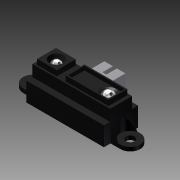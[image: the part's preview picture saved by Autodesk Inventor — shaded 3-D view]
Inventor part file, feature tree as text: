
AUTODESK INVENTOR PART (.ipt)
format: ipt  version: 2012 (Build 160160000, 160)  size: 424,448 bytes
history: native  units: mm
features: sketch x27, extrude x17, plane x3, mirror x3, revolve x3, loft x2, projected_geometry x2
ambient origin geometry x8: Origin, YZ Plane, XZ Plane, XY Plane, X Axis, Y Axis, Z Axis, Center Point
bodies: Solid1 (feature_tree)
feature tree (57):
  extrude  "Extrusion1"  Depth=13.0mm
  extrude  "Extrusion2"  Depth=4.2mm
  extrude  "Extrusion3"  Depth=6.3mm TaperAngle=0.0deg
  extrude  "Extrusion4"  Depth=7.2mm
  extrude  "Extrusion5"  Depth=1.2mm
  extrude  "Extrusion6"  Depth=2.0mm TaperAngle=0.0deg
  extrude  "Extrusion7"  Depth=7.5mm
  sketch  "Sketch8"  dims[d18=2.0mm d19=0.0mm d20=6.3mm d21=0.0mm]
  sketch  "Sketch9"  dims[d22=3.75mm d23=3.2mm]
  plane  "Work Plane1"
  extrude  "Extrusion8"  Depth=6.3mm TaperAngle=0.0deg
  extrude  "Extrusion9"  Depth=3.2mm
  plane  "Work Plane2"
  mirror  "Mirror1"
  loft  "Loft1"
  sketch  "Sketch14"  dims[d36=0.0mm d37=90.0deg d38=90.0deg]
  plane  "Work Plane3"
  revolve  "Revolution1"  [1 undecoded]
  revolve  "Revolution2"  [1 undecoded]
  extrude  "Extrusion10"  TaperAngle=0.0deg  [1 undecoded]
  loft  "Loft2"
  extrude  "Extrusion11"  Depth=0.5mm
  revolve  "Revolution3"  [1 undecoded]
  extrude  "Extrusion12"  Depth=1.5mm TaperAngle=0.0deg
  extrude  "Extrusion13"  Depth=4.2mm
  mirror  "Mirror2"
  extrude  "Extrusion14"  TaperAngle=0.0deg  [1 undecoded]
  extrude  "Extrusion15"  TaperAngle=90.0deg  [1 undecoded]
  mirror  "Mirror3"
  extrude  "Extrusion16"  Depth=5.05mm
  extrude  "Extrusion17"  Depth=5.9mm TaperAngle=0.0deg
  sketch  "Sketch1"  dims[d0=29.5mm d1=13.0mm]
  sketch  "Sketch2"  dims[d2=13.5mm d3=0.0mm d4=4.2mm]
  sketch  "Sketch3"  dims[d5=8.4mm d6=6.3mm d7=0.0mm]
  sketch  "Sketch4"  dims[d8=3.6mm d9=7.2mm]
  sketch  "Sketch5"  dims[d10=2.0mm d11=0.0mm d12=1.2mm]
  sketch  "Sketch6"  dims[d13=1.2mm d14=2.0mm d15=0.0mm]
  sketch  "Sketch7"  dims[d16=16.3mm d17=7.5mm]
  sketch  "Sketch10"  dims[d24=1.5mm d25=0.0mm d26=2.6mm]
  sketch  "Sketch11"  dims[d27=5.0mm d28=1.5mm d29=0.0mm]
  sketch  "Sketch12"  dims[d30=1.5mm d31=0.0mm d32=1.0mm]
  sketch  "Sketch13"  dims[d33=3.5mm d34=0.0mm d35=90.0deg]
  sketch  "Sketch15"  dims[d39=90.0deg d40=0.5mm]
  sketch  "Sketch16"  dims[d41=0.5mm d42=0.5mm]
  sketch  "Sketch17"  dims[d43=0.5mm d44=1.5mm d45=0.0mm]
  sketch  "Sketch18"  dims[d46=6.2mm d47=4.2mm]
  projected_geometry  "Projected Loop1"
  sketch  "Sketch19"  dims[d48=0.0mm d49=90.0deg d50=0.0mm d51=90.0deg]
  sketch  "Sketch20"  dims[d52=0.5mm d53=0.0mm d54=90.0deg]
  sketch  "Sketch21"  dims[d55=3.3mm d56=5.05mm]
  projected_geometry  "Projected Loop2"
  sketch  "Sketch22"  dims[d57=10.1mm d58=5.9mm d59=0.0mm]
  sketch  "Sketch23"  dims[d60=4.0mm]
  sketch  "Sketch24"  dims[d61=5.3mm d62=0.0mm]
  sketch  "Sketch25"  dims[d65=0.5mm]
  sketch  "Sketch26"  dims[d66=0.5mm]
  sketch  "Sketch27"  dims[d67=4.5mm d68=0.0mm d69=2.0mm d70=0.7mm d71=0.5mm d72=0.0mm d73=0.75mm d74=4.0mm d75=1.5mm d76=0.5mm d77=0.0mm d78=45.0deg d79=0.5mm d80=0.5mm d81=3.3mm d82=0.0mm]
note: 6 required parameter values undecoded (feature->parameter linkage not recoverable at this tier; creation-order binding heuristic only, values carry confidence <= 0.55)